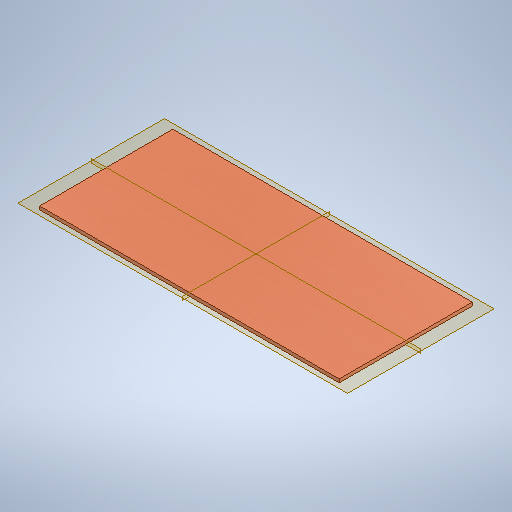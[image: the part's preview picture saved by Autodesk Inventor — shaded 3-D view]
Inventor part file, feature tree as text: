
AUTODESK INVENTOR PART (.ipt)
format: ipt  version: 2025.2 (Build 292293000, 293)  size: 268,800 bytes
history: native  units: mm
features: other x1, extrude x1, sketch x1
ambient origin geometry x8: Origin, YZ Plane, XZ Plane, XY Plane, X Axis, Y Axis, Z Axis, Center Point
bodies: Body1 (feature_tree)
feature tree (3):
  other  "Sólido1"
  extrude  "Extrusão1"  Depth=800.0mm
  sketch  "Esboço1"  dims[d0=1800.0mm d1=800.0mm d2=20.0mm d3=0.0mm]
